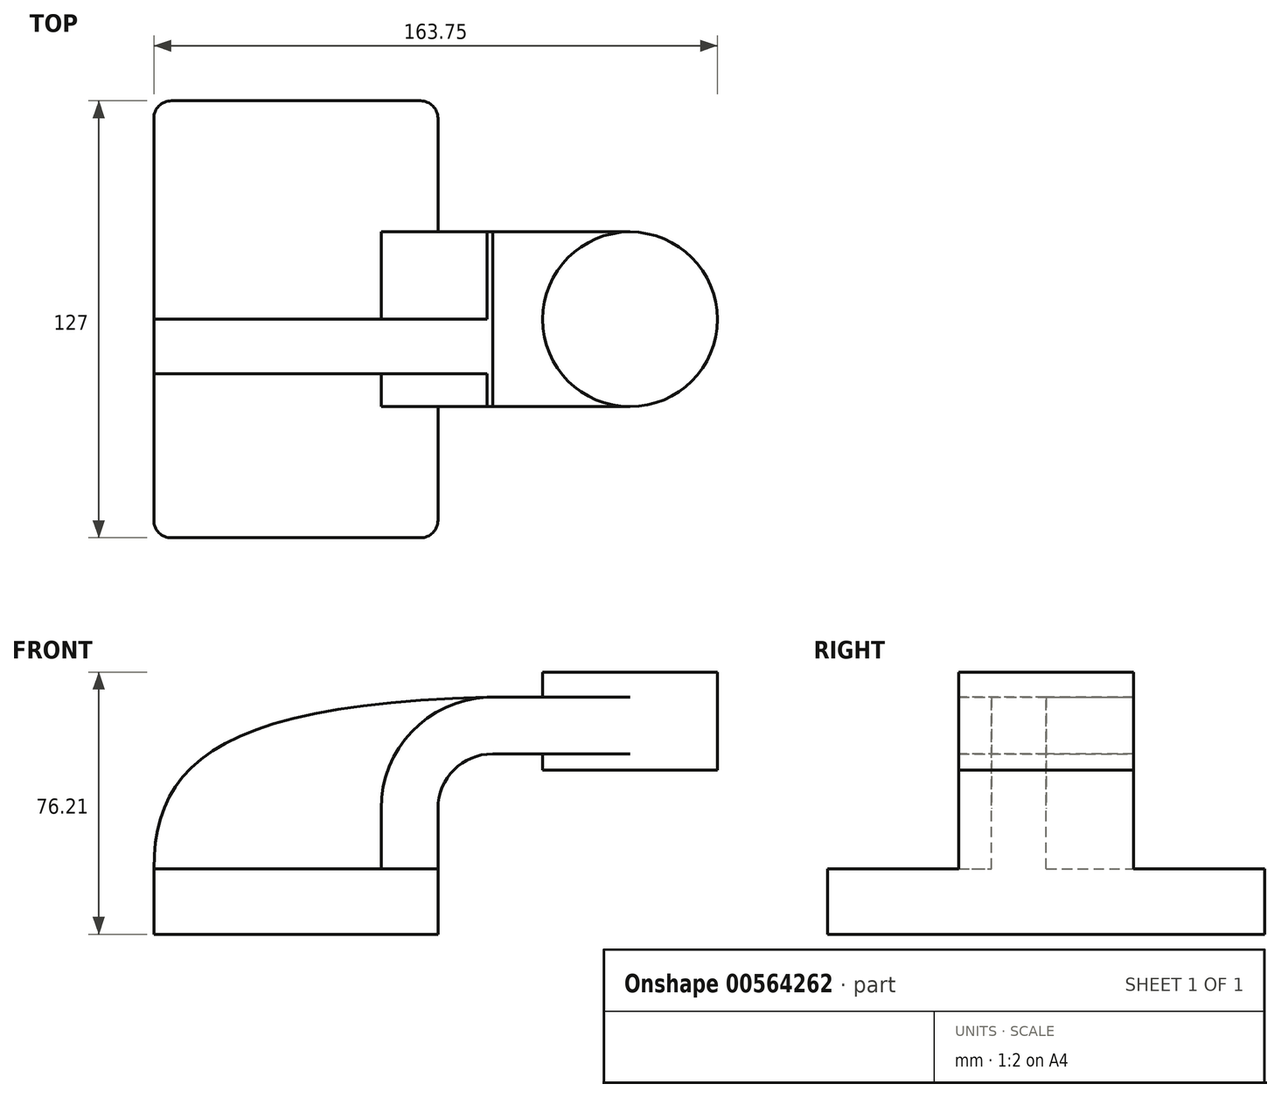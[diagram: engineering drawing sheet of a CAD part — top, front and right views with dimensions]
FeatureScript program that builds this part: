
annotation { "Feature Type Name" : "Feature", "Feature Type Description" : "" }
export const myFeature = defineFeature(function(context is Context, id is Id, definition is map)
    precondition{}
    {
        {
            var Q0;
            Q0=qCreatedBy(makeId("Front.planeOp"),FACE);
            var sketch = newSketch(context, id + "F0", { "sketchPlane" : qUnion([Q0])});
            skLineSegment(sketch, "E0.bottom", {"start": v(41.28, -9.52) * mm, "end": v(-41.27, -9.52) * mm});
            skLineSegment(sketch, "E0.top", {"start": v(41.27, 9.53) * mm, "end": v(-41.28, 9.53) * mm});
            skLineSegment(sketch, "E0.left", {"start": v(41.28, -9.52) * mm, "end": v(41.28, 9.53) * mm});
            skLineSegment(sketch, "E0.right", {"start": v(-41.27, -9.53) * mm, "end": v(-41.28, 9.52) * mm});
            skPoint(sketch, "E0.middle", {"position": v(0, 0) * mm});
            skLineSegment(sketch, "E1", {"start": v(41.27, 9.53) * mm, "end": v(41.27, 27) * mm});
            skArc(sketch, "E2", {"start": v(41.27, 27) * mm, "mid": v(45.92, 38.23) * mm, "end": v(57.15, 42.88) * mm});
            skPoint(sketch, "E3.firstSnap0", {"position": v(71.67, 42.88) * mm});
            skPoint(sketch, "E3.oppositeSnap0", {"position": v(45.92, 38.23) * mm});
            skLineSegment(sketch, "E3.bottom", {"start": v(71.67, 66.68) * mm, "end": v(122.47, 66.68) * mm});
            skLineSegment(sketch, "E3.top", {"start": v(71.67, 38.23) * mm, "end": v(122.47, 38.23) * mm});
            skLineSegment(sketch, "E3.left", {"start": v(71.67, 66.68) * mm, "end": v(71.67, 38.23) * mm});
            skLineSegment(sketch, "E3.right", {"start": v(122.47, 66.68) * mm, "end": v(122.47, 38.23) * mm});
            skLineSegment(sketch, "E4", {"start": v(57.15, 42.88) * mm, "end": v(97.07, 42.88) * mm});
            skPoint(sketch, "E4.endSnap0", {"position": v(97.07, 38.23) * mm});
            skLineSegment(sketch, "E5.0", {"start": v(57.15, 59.39) * mm, "end": v(97.07, 59.39) * mm});
            skArc(sketch, "E5.1", {"start": v(24.76, 27) * mm, "mid": v(34.25, 49.9) * mm, "end": v(57.15, 59.39) * mm});
            skLineSegment(sketch, "E5.2", {"start": v(24.76, 9.53) * mm, "end": v(24.76, 27) * mm});
            skLineSegment(sketch, "E6", {"start": v(97.07, 38.23) * mm, "end": v(97.07, 66.68) * mm});
            skFitSpline(sketch, "E7", {"points": [v(-41.28, 9.53) * mm, v(57.15, 59.39) * mm], "startDerivative": vector(0.5, 90.47) * mm, "endDerivative": vector(241.14, 5.82) * mm});
            skSolve(sketch);
        }
        {
            var Q0;
            Q0=makeQuery(id+"F0.imprint","IMPRINT",FACE,{"disambiguationData":[TD([[makeQuery(id+"F0.imprint","IMPRINT",EDGE,{"derivedFrom":sQuery(id+"F0.wireOp",EDGE,"E0.bottom")}),-1.0]])]});
            extrude(context, id + "F1", {"entities" : qUnion([Q0]), "endBound" : BoundingType.SYMMETRIC, "depth" : 127 * mm, "offsetDistance" : 25.4 * mm});
        }
        {
            var Q0;
            {var subQ5=sQuery(id+"F0.wireOp",EDGE,"E1");Q0=makeQuery(id+"F0.imprint","IMPRINT",FACE,{"disambiguationData":[TD([[makeQuery(id+"F0.imprint","IMPRINT",EDGE,{"derivedFrom":subQ5}),1.0]])]});}
            var Q1;
            {var subQ0=sQuery(id+"F0.wireOp",EDGE,"E5.0");var subQ1=sQuery(id+"F0.wireOp",EDGE,"E3.left");var subQ2=makeQuery(id+"F0.imprint","INTERSECT",VERTEX,{"derivedFrom":[subQ1,subQ0]});Q1=makeQuery(id+"F0.imprint","IMPRINT",FACE,{"disambiguationData":[TD([[makeQuery(id+"F0.imprint","IMPRINT",EDGE,{"disambiguationData":[TD([[subQ2,-1.0]])],"derivedFrom":subQ1}),1.0]])]});}
            extrude(context, id + "F2", {"entities" : qUnion([Q0, Q1]), "operationType" : NewBodyOperationType.ADD, "endBound" : BoundingType.SYMMETRIC, "depth" : 50.8 * mm, "offsetDistance" : 25.4 * mm});
        }
        {
            var Q0;
            {var subQ3=sQuery(id+"F0.wireOp",EDGE,"E5.2");Q0=makeQuery(id+"F0.imprint","IMPRINT",FACE,{"disambiguationData":[TD([[makeQuery(id+"F0.imprint","IMPRINT",EDGE,{"derivedFrom":subQ3}),1.0]])]});}
            extrude(context, id + "F3", {"entities" : qUnion([Q0]), "operationType" : NewBodyOperationType.ADD, "depth" : 15.88 * mm, "offsetDistance" : 25.4 * mm});
        }
        {
            var Q0;
            {var subQ4=sQuery(id+"F0.wireOp",EDGE,"E3.right");Q0=makeQuery(id+"F0.imprint","IMPRINT",FACE,{"disambiguationData":[TD([[makeQuery(id+"F0.imprint","IMPRINT",EDGE,{"derivedFrom":subQ4}),-1.0]])]});}
            var Q1;
            Q1=sQuery(id+"F0.wireOp",EDGE,"E6");
            revolve(context, id + "F4", {"operationType" : NewBodyOperationType.ADD, "entities" : qUnion([Q0]), "axis" : qUnion([Q1]), "revolveType" : RevolveType.FULL});
        }
        {
            var Q0;
            Q0=makeQuery(id+"F1.opExtrude","CAP_EDGE",EDGE,{"disambiguationData":[OSD([sQuery(id+"F0.wireOp",EDGE,"E0.left")])],"isStart":false});
            var Q1;
            Q1=makeQuery(id+"F1.opExtrude","CAP_EDGE",EDGE,{"disambiguationData":[OSD([sQuery(id+"F0.wireOp",EDGE,"E0.right")])],"isStart":false});
            var Q2;
            Q2=makeQuery(id+"F1.opExtrude","CAP_EDGE",EDGE,{"disambiguationData":[OSD([sQuery(id+"F0.wireOp",EDGE,"E0.left")])],"isStart":true});
            var Q3;
            Q3=makeQuery(id+"F1.opExtrude","CAP_EDGE",EDGE,{"disambiguationData":[OSD([sQuery(id+"F0.wireOp",EDGE,"E0.right")])],"isStart":true});
            fillet(context, id + "F5", {"entities" : qUnion([Q0, Q1, Q2, Q3]), "radius" : 5.08 * mm, "tangentPropagation" : true, "allowEdgeOverflow" : false});
        }
    });
